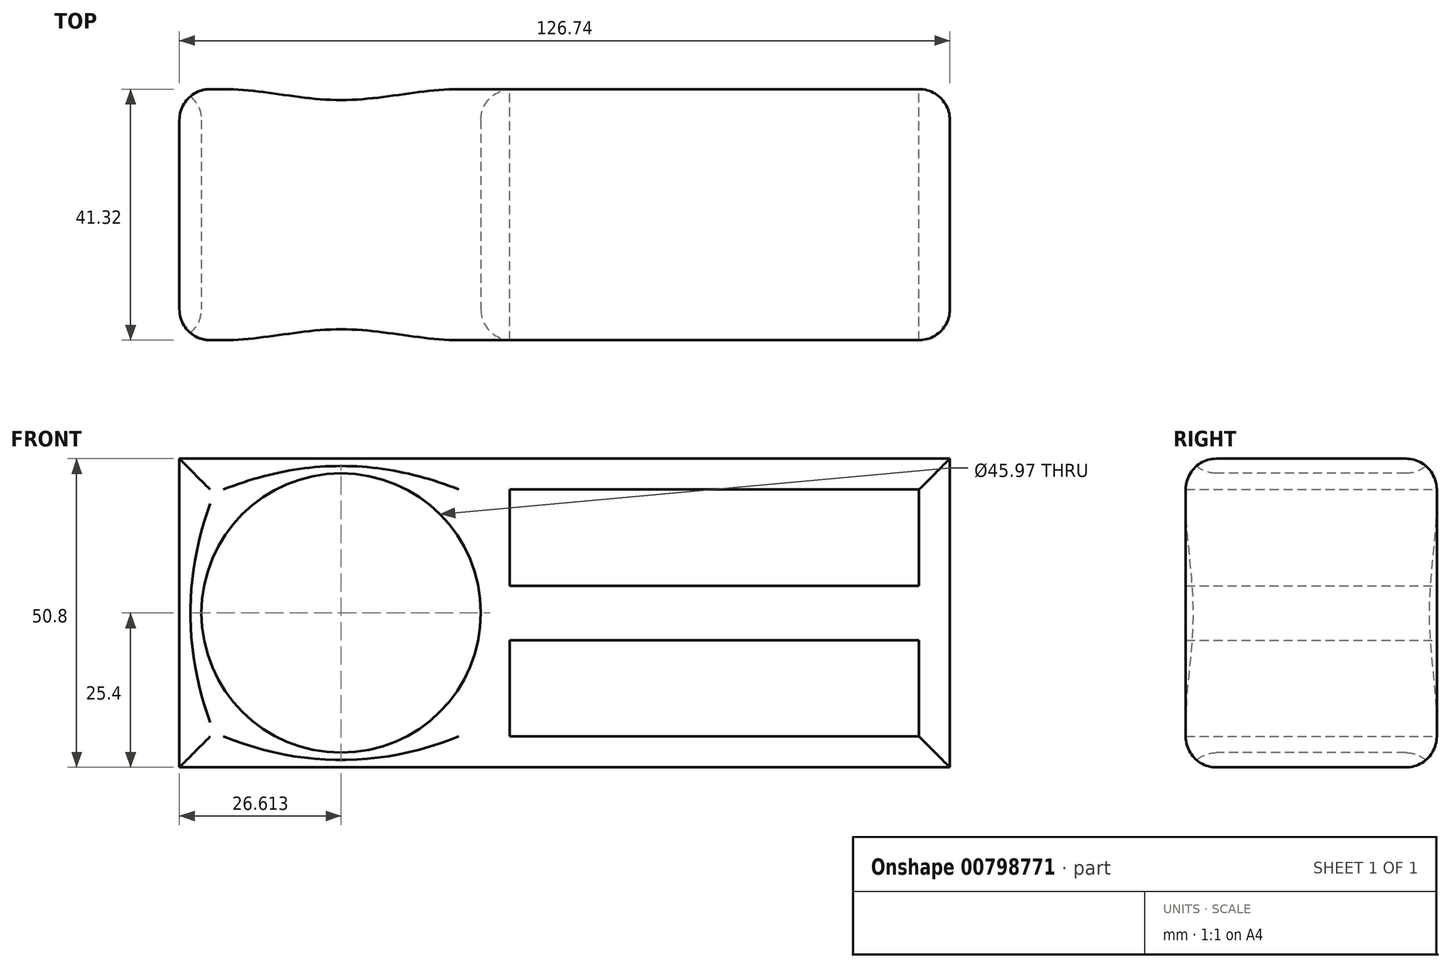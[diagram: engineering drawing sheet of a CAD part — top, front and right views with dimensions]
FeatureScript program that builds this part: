
annotation { "Feature Type Name" : "Feature", "Feature Type Description" : "" }
export const myFeature = defineFeature(function(context is Context, id is Id, definition is map)
    precondition{}
    {
        {
            var Q0;
            Q0=qCreatedBy(makeId("Top.planeOp"),FACE);
            var sketch = newSketch(context, id + "F0", { "sketchPlane" : qUnion([Q0])});
            skLineSegment(sketch, "E0.bottom", {"start": v(-63.37, 20.66) * mm, "end": v(63.37, 20.66) * mm});
            skLineSegment(sketch, "E0.top", {"start": v(-63.37, -20.66) * mm, "end": v(63.37, -20.66) * mm});
            skLineSegment(sketch, "E0.left", {"start": v(-63.37, 20.66) * mm, "end": v(-63.37, -20.66) * mm});
            skLineSegment(sketch, "E0.right", {"start": v(63.37, 20.66) * mm, "end": v(63.37, -20.66) * mm});
            skPoint(sketch, "E0.middle", {"position": v(0, 0) * mm});
            skSolve(sketch);
        }
        {
            var Q0;
            Q0=makeQuery(id+"F0.imprint","IMPRINT",FACE,{"disambiguationData":[TD([[makeQuery(id+"F0.imprint","IMPRINT",EDGE,{"derivedFrom":sQuery(id+"F0.wireOp",EDGE,"E0.bottom")}),-1.0]])]});
            extrude(context, id + "F1", {"entities" : qUnion([Q0]), "endBound" : BoundingType.SYMMETRIC, "depth" : 50.8 * mm, "offsetDistance" : 25.4 * mm});
        }
        {
            var Q0;
            Q0=makeQuery(id+"F1.opExtrude","SWEPT_FACE",FACE,{"disambiguationData":[OSD([sQuery(id+"F0.wireOp",EDGE,"E0.top")])]});
            var sketch = newSketch(context, id + "F2", { "sketchPlane" : qUnion([Q0])});
            skLineSegment(sketch, "E1", {"start": v(-63.37, 25.4) * mm, "end": v(-36.76, 25.4) * mm});
            skLineSegment(sketch, "E2", {"start": v(-36.76, 25.4) * mm, "end": v(-36.76, -25.4) * mm, "construction": true});
            skCircle(sketch, "E3", {"center": v(-36.76, 0) * mm, "radius": 22.99 * mm});
            skSolve(sketch);
        }
        {
            var Q0;
            Q0=makeQuery(id+"F2.imprint","IMPRINT",FACE,{"disambiguationData":[TD([[makeQuery(id+"F2.imprint","IMPRINT",EDGE,{"derivedFrom":sQuery(id+"F2.wireOp",EDGE,"E3")}),1.0]])]});
            extrude(context, id + "F3", {"entities" : qUnion([Q0]), "operationType" : NewBodyOperationType.REMOVE, "endBound" : BoundingType.THROUGH_ALL, "oppositeDirection" : true, "depth" : 50.8 * mm, "offsetDistance" : 25.4 * mm});
        }
        {
            var Q0;
            Q0=makeQuery(id+"F1.opExtrude","SWEPT_FACE",FACE,{"disambiguationData":[OSD([sQuery(id+"F0.wireOp",EDGE,"E0.top")])]});
            fillet(context, id + "F4", {"entities" : qUnion([Q0]), "radius" : 5.08 * mm, "tangentPropagation" : true, "allowEdgeOverflow" : false});
        }
        {
            var Q0;
            Q0=makeQuery(id+"F1.opExtrude","SWEPT_FACE",FACE,{"disambiguationData":[OSD([sQuery(id+"F0.wireOp",EDGE,"E0.bottom")])]});
            fillet(context, id + "F5", {"entities" : qUnion([Q0]), "radius" : 5.08 * mm, "tangentPropagation" : true, "allowEdgeOverflow" : false});
        }
        {
            var Q0;
            Q0=makeQuery(id+"F5.opFillet","SPLIT",FACE,{"disambiguationData":[OD(2.0)],"derivedFrom":makeQuery(id+"F1.opExtrude","SWEPT_FACE",FACE,{"disambiguationData":[OSD([sQuery(id+"F0.wireOp",EDGE,"E0.bottom")])]})});
            var sketch = newSketch(context, id + "F6", { "sketchPlane" : qUnion([Q0])});
            skLineSegment(sketch, "E4.bottom", {"start": v(-58.3, -20.32) * mm, "end": v(9.05, -20.32) * mm});
            skLineSegment(sketch, "E4.top", {"start": v(-58.3, -4.47) * mm, "end": v(9.05, -4.47) * mm});
            skLineSegment(sketch, "E4.left", {"start": v(-58.3, -20.32) * mm, "end": v(-58.3, -4.47) * mm});
            skLineSegment(sketch, "E4.right", {"start": v(9.05, -20.32) * mm, "end": v(9.05, -4.47) * mm});
            skLineSegment(sketch, "E5.bottom", {"start": v(-58.3, 20.32) * mm, "end": v(9.05, 20.32) * mm});
            skLineSegment(sketch, "E5.top", {"start": v(-58.3, 4.47) * mm, "end": v(9.05, 4.47) * mm});
            skLineSegment(sketch, "E5.left", {"start": v(-58.3, 20.32) * mm, "end": v(-58.3, 4.47) * mm});
            skLineSegment(sketch, "E5.right", {"start": v(9.05, 20.32) * mm, "end": v(9.05, 4.47) * mm});
            skSolve(sketch);
        }
        {
            var Q0;
            Q0=makeQuery(id+"F6.imprint","IMPRINT",FACE,{"disambiguationData":[TD([[makeQuery(id+"F6.imprint","IMPRINT",EDGE,{"derivedFrom":sQuery(id+"F6.wireOp",EDGE,"E5.bottom")}),1.0]])]});
            var Q1;
            Q1=makeQuery(id+"F6.imprint","IMPRINT",FACE,{"disambiguationData":[TD([[makeQuery(id+"F6.imprint","IMPRINT",EDGE,{"derivedFrom":sQuery(id+"F6.wireOp",EDGE,"E4.bottom")}),1.0]])]});
            extrude(context, id + "F7", {"entities" : qUnion([Q0, Q1]), "operationType" : NewBodyOperationType.REMOVE, "endBound" : BoundingType.THROUGH_ALL, "oppositeDirection" : true, "depth" : 25.4 * mm, "offsetDistance" : 25.4 * mm});
        }
    });
